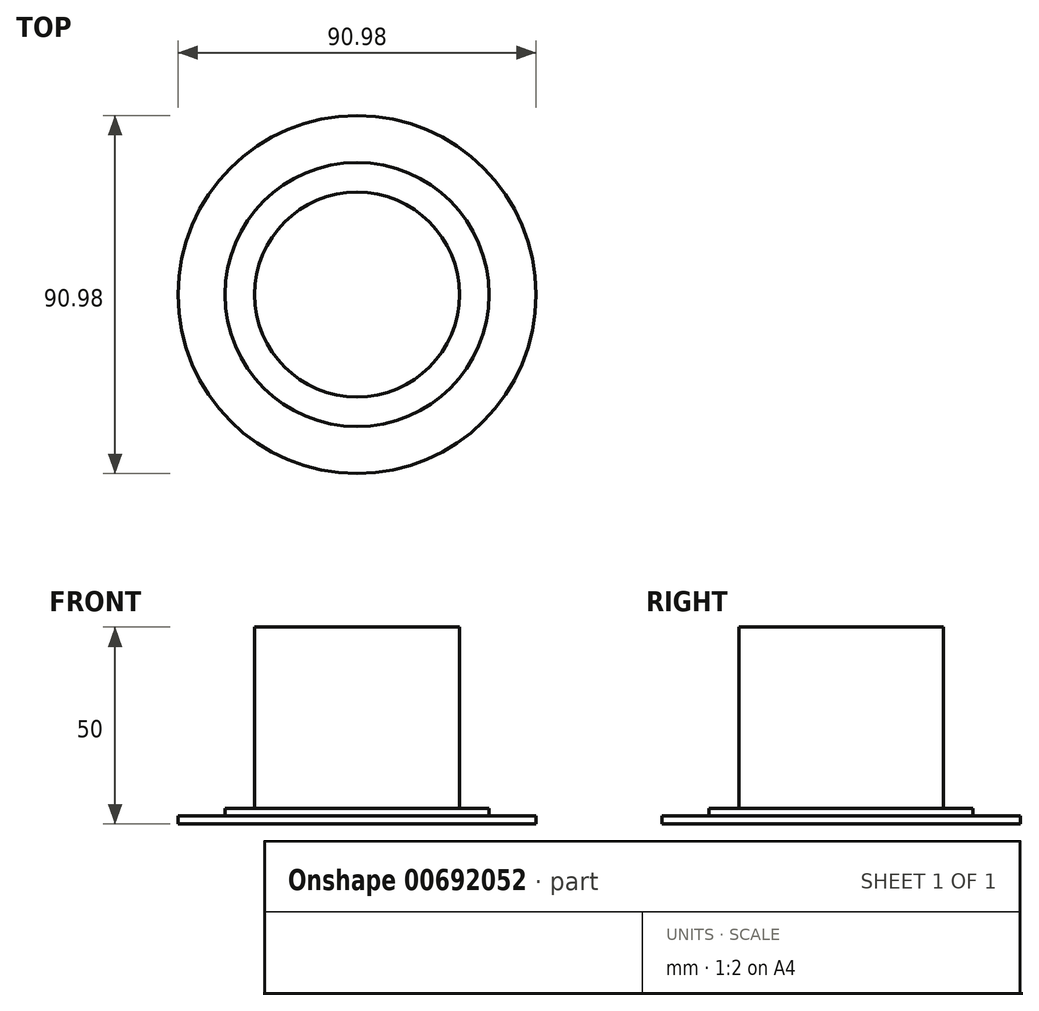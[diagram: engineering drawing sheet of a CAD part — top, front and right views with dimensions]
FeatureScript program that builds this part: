
annotation { "Feature Type Name" : "Feature", "Feature Type Description" : "" }
export const myFeature = defineFeature(function(context is Context, id is Id, definition is map)
    precondition{}
    {
        {
            var Q0;
            Q0=qCreatedBy(makeId("Top.planeOp"),FACE);
            var sketch = newSketch(context, id + "F0", { "sketchPlane" : qUnion([Q0])});
            skCircle(sketch, "E0", {"center": v(0, 0) * mm, "radius": 45.5 * mm});
            skSolve(sketch);
        }
        {
            var Q0;
            Q0=qCreatedBy(makeId("Top.planeOp"),FACE);
            var sketch = newSketch(context, id + "F1", { "sketchPlane" : qUnion([Q0])});
            skCircle(sketch, "E1", {"center": v(0, 0) * mm, "radius": 33.53 * mm});
            skSolve(sketch);
        }
        {
            var Q0;
            Q0=qCreatedBy(makeId("Top.planeOp"),FACE);
            var sketch = newSketch(context, id + "F2", { "sketchPlane" : qUnion([Q0])});
            skCircle(sketch, "E2", {"center": v(0, 0) * mm, "radius": 26.02 * mm});
            skSolve(sketch);
        }
        {
            var Q0;
            Q0 = qSketchRegion(id + "F0", true);
            extrude(context, id + "F3", {"entities" : qUnion([Q0]), "depth" : 2 * mm, "offsetDistance" : 25 * mm});
        }
        {
            var Q0;
            Q0 = qSketchRegion(id + "F1", true);
            extrude(context, id + "F4", {"entities" : qUnion([Q0]), "operationType" : NewBodyOperationType.ADD, "depth" : 4 * mm, "offsetDistance" : 25 * mm});
        }
        {
            var Q0;
            Q0 = qSketchRegion(id + "F2", true);
            extrude(context, id + "F5", {"entities" : qUnion([Q0]), "operationType" : NewBodyOperationType.ADD, "depth" : 50 * mm, "offsetDistance" : 25 * mm});
        }
    });
